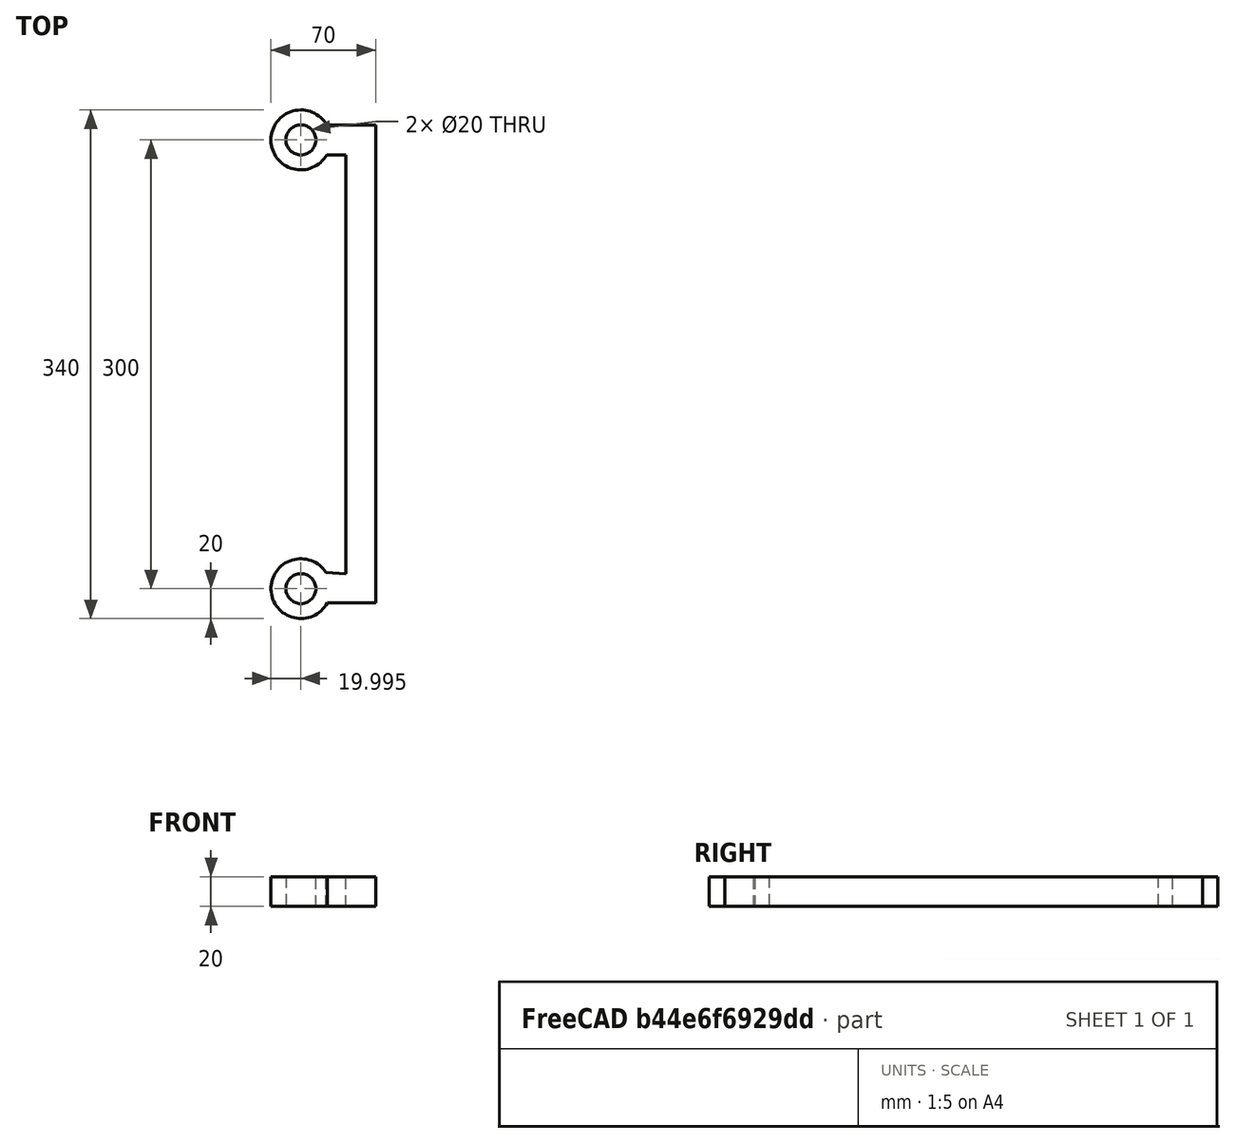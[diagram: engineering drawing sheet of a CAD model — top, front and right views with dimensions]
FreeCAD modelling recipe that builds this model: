
FCSTD DOCUMENT  (FreeCAD 0.20R29177 +426 (Git))
Label: rotary-branch-2
License: All rights reserved
LicenseURL: http://en.wikipedia.org/wiki/All_rights_reserved
objects: Sketcher::SketchObject×1, PartDesign::Body×1, Part::Extrusion×1
note: 3 computed .brp shape members not serialized (recipe doc carries the construction recipe); baked Part::Feature solids carry a one-line shape summary decoded from their .brp

FEATURE [Sketcher::SketchObject] Sketch
  FullyConstrained = false
  MapMode = 5
  Support = -> [XY_Plane]
  sketch-geometry (18):
    g0: LineSegment StartX=11.6776 StartY=0.722876 StartZ=0 EndX=24.7951 EndY=0 EndZ=0
    g1: LineSegment StartX=24.7951 StartY=280 StartZ=0 EndX=24.7951 EndY=0 EndZ=0
    g2: LineSegment StartX=24.7951 StartY=280 StartZ=0 EndX=12.1156 EndY=280 EndZ=0
    g3: LineSegment StartX=12.1156 StartY=300 StartZ=0 EndX=44.7951 EndY=300 EndZ=0
    g4: LineSegment StartX=44.7951 StartY=300 StartZ=0 EndX=44.7951 EndY=-19.5964 EndZ=0
    g5: LineSegment StartX=44.7951 StartY=-19.5964 StartZ=0 EndX=12.3424 EndY=-19.5964 EndZ=0
    g6: LineSegment StartX=24.7951 StartY=280 StartZ=0 EndX=24.7951 EndY=300 EndZ=0
    g7: LineSegment StartX=24.7951 StartY=280 StartZ=0 EndX=44.7951 EndY=280 EndZ=0
    g8: ArcOfCircle CenterX=-5.20491 CenterY=-10 CenterZ=0 NormalX=0 NormalY=0 NormalZ=1 AngleXU=0 Radius=20 StartAngle=0.565862 EndAngle=5.78273
    g9: LineSegment StartX=0 StartY=0 StartZ=0 EndX=-5.20491 EndY=-10 EndZ=0
    g10: LineSegment StartX=-5.20491 StartY=-10 StartZ=0 EndX=0 EndY=-20 EndZ=0
    g11: Circle CenterX=-5.20491 CenterY=-10 CenterZ=0 NormalX=0 NormalY=0 NormalZ=1 AngleXU=0 Radius=10
    g12: LineSegment StartX=-5.20491 StartY=-10 StartZ=0 EndX=-5.20491 EndY=290 EndZ=0
    g13: ArcOfCircle CenterX=-5.20491 CenterY=290 CenterZ=0 NormalX=0 NormalY=0 NormalZ=1 AngleXU=0 Radius=20 StartAngle=0.523599 EndAngle=5.75959
    g14: Circle CenterX=-5.20491 CenterY=290 CenterZ=0 NormalX=0 NormalY=0 NormalZ=1 AngleXU=0 Radius=10
    g15: LineSegment StartX=12.1156 StartY=300 StartZ=0 EndX=-5.20491 EndY=290 EndZ=0
    g16: LineSegment StartX=12.1156 StartY=280 StartZ=0 EndX=-5.20491 EndY=290 EndZ=0
    g17: LineSegment StartX=-5.20491 StartY=290 StartZ=0 EndX=24.7951 EndY=290 EndZ=0
  constraints (47):
    c: PointOnObject(g0,g-1)
    c: Coincident(g1,g0)
    c: Vertical(g1)
    c: Coincident(g2,g1)
    c: Horizontal(g2)
    c: Horizontal(g3)
    c: Coincident(g4,g3)
    c: Vertical(g4)
    c: Coincident(g5,g4)
    c: PointOnObject(g10,g-2)
    c: Horizontal(g5)
    c: Coincident(g6,g1)
    c: PointOnObject(g6,g3)
    c: Vertical(g6)
    c: Coincident(g7,g1)
    c: PointOnObject(g7,g4)
    c: Horizontal(g7)
    c: Equal(g6,g7)
    c: Coincident(g9,g-1)
    c: Coincident(g9,g8)
    c: Coincident(g10,g8)
    c: Equal(g10,g9)
    c: Coincident(g11,g8)
    c: Diameter(g11) = 20
    c: Diameter(g8) = 40
    c: Coincident(g8,g0)
    c: Coincident(g5,g8)
    c: DistanceX(g8) = -5.20491
    c: DistanceY(g8) = -10
    c: Coincident(g12,g8)
    c: Vertical(g12)
    c: Equal(g13,g8)
    c: Coincident(g3,g13)
    c: Coincident(g2,g13)
    c: Coincident(g14,g13)
    c: Diameter(g14) = 20
    c: Coincident(g12,g13)
    c: Coincident(g15,g3)
    c: Coincident(g15,g13)
    c: Coincident(g16,g2)
    c: Coincident(g16,g13)
    c: Coincident(g17,g13)
    c: Horizontal(g17)
    c: Symmetric(g1,g6,g17)
    c: DistanceY(g12,g12) = 300
    c: DistanceX(g7,g7) = 20
    c: DistanceX(g13,g3) = 50
FEATURE [PartDesign::Body] Body
  Group = -> [Sketch]
  Origin = -> Origin
FEATURE [Part::Extrusion] Extrude
  Base = -> Sketch
  Dir = (0,0,1)
  DirMode = 2
  FaceMakerClass = Part::FaceMakerBullseye
  LengthFwd = 20
  LengthRev = 0
  Solid = true
  Symmetric = false
